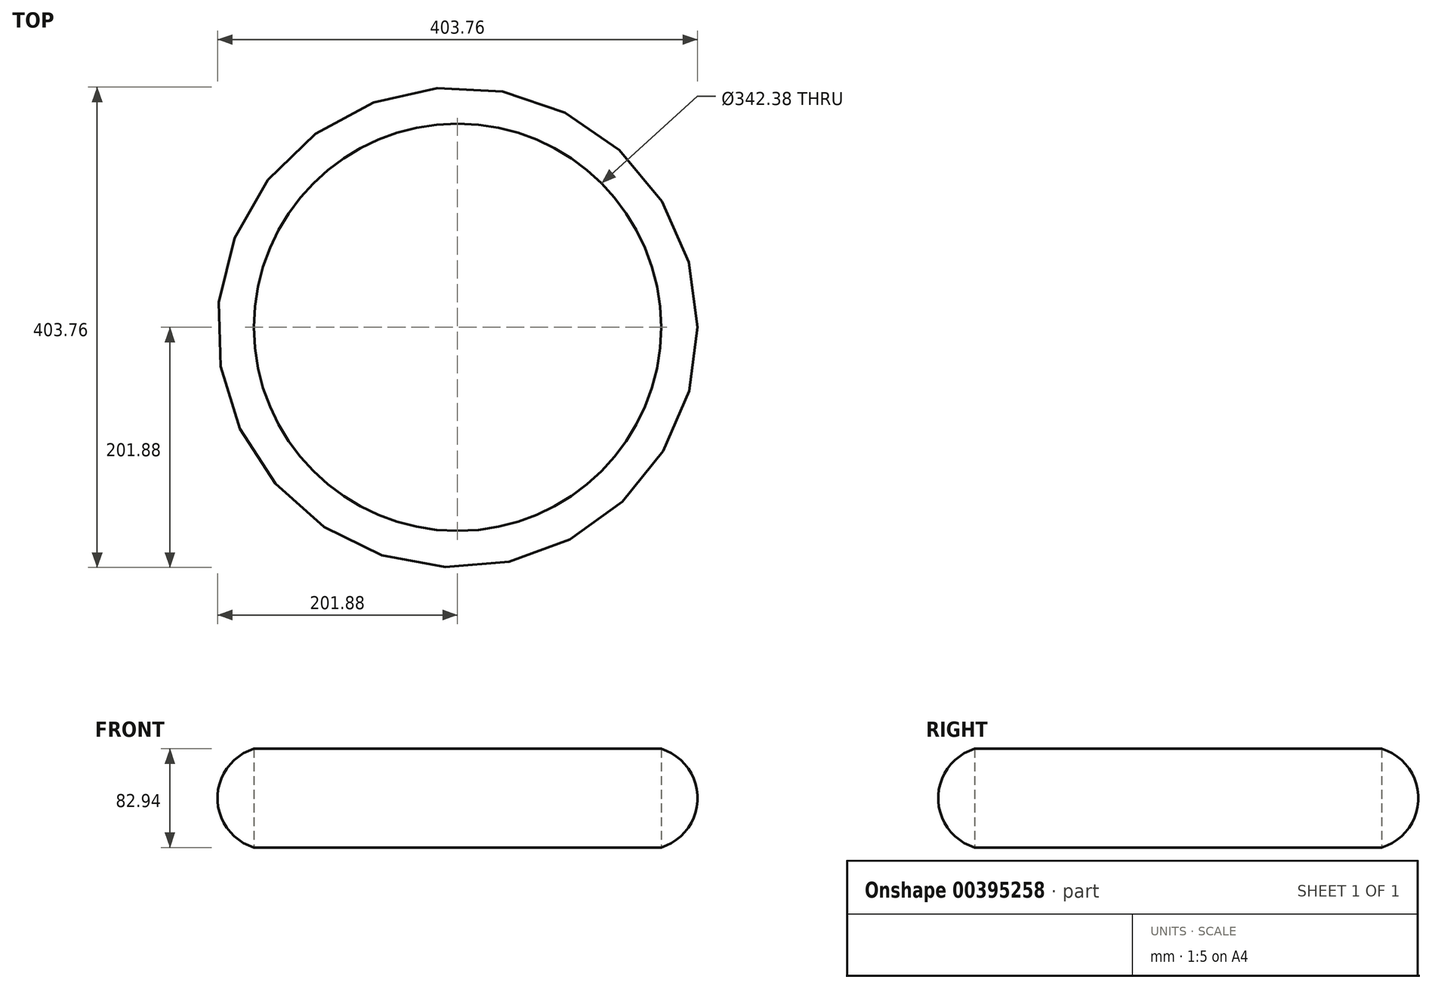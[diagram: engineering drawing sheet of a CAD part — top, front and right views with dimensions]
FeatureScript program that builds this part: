
annotation { "Feature Type Name" : "Feature", "Feature Type Description" : "" }
export const myFeature = defineFeature(function(context is Context, id is Id, definition is map)
    precondition{}
    {
        {
            var Q0;
            Q0=qCreatedBy(makeId("Top.planeOp"),FACE);
            var sketch = newSketch(context, id + "F0", { "sketchPlane" : qUnion([Q0])});
            skCircle(sketch, "E0", {"center": v(0, 0) * mm, "radius": 206.66 * mm});
            skSolve(sketch);
        }
        {
            var Q0;
            Q0=qCreatedBy(makeId("Right.planeOp"),FACE);
            var sketch = newSketch(context, id + "F1", { "sketchPlane" : qUnion([Q0])});
            skCircle(sketch, "E1", {"center": v(-158.53, 0) * mm, "radius": 43.36 * mm});
            skSolve(sketch);
        }
        {
            var Q0;
            Q0=makeQuery(id+"F1.imprint","IMPRINT",FACE,{"disambiguationData":[TD([[makeQuery(id+"F1.imprint","IMPRINT",EDGE,{"derivedFrom":sQuery(id+"F1.wireOp",EDGE,"E1")}),1.0]])]});
            var Q1;
            Q1=sQuery(id+"F0.wireOp",EDGE,"E0");
            sweep(context, id + "F2", {"profiles" : qUnion([Q0]), "path" : qUnion([Q1])});
        }
        {
            var Q0;
            Q0=qCreatedBy(makeId("Top.planeOp"),FACE);
            var sketch = newSketch(context, id + "F3", { "sketchPlane" : qUnion([Q0])});
            skCircle(sketch, "E2", {"center": v(0, 0) * mm, "radius": 171.19 * mm});
            skSolve(sketch);
        }
        {
            var Q0;
            Q0 = qSketchRegion(id + "F3", true);
            extrude(context, id + "F4", {"entities" : qUnion([Q0]), "operationType" : NewBodyOperationType.REMOVE, "depth" : 439.93 * mm, "hasSecondDirection" : true, "secondDirectionOppositeDirection" : true, "secondDirectionDepth" : 259.08 * mm});
        }
    });
